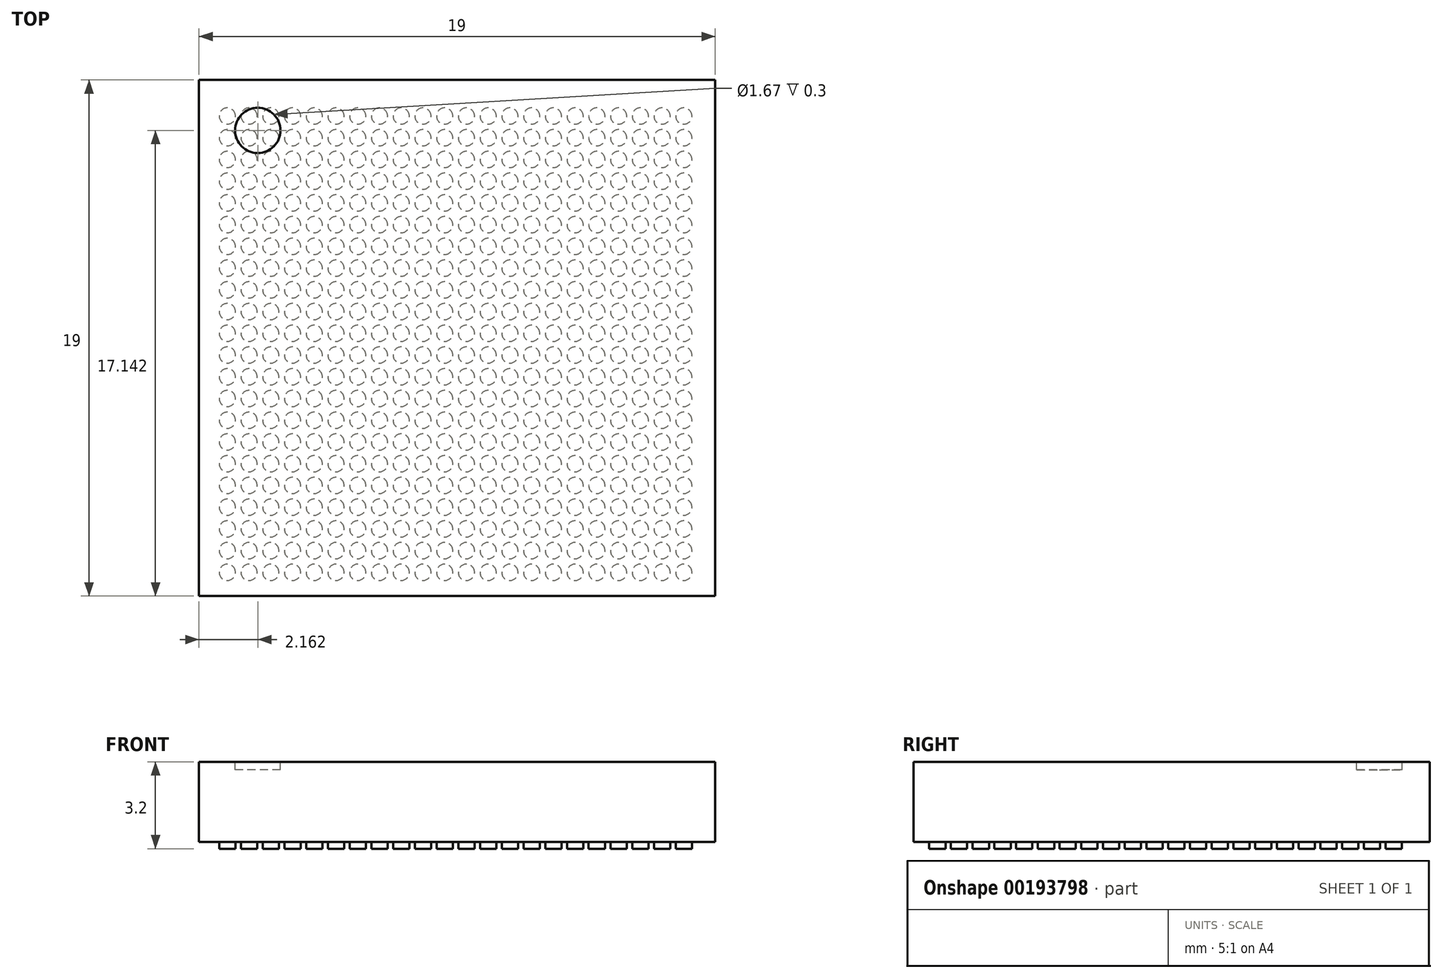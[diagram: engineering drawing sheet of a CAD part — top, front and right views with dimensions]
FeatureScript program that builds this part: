
annotation { "Feature Type Name" : "Feature", "Feature Type Description" : "" }
export const myFeature = defineFeature(function(context is Context, id is Id, definition is map)
    precondition{}
    {
        {
            var Q0;
            Q0=qCreatedBy(makeId("Top.planeOp"),FACE);
            var sketch = newSketch(context, id + "F0", { "sketchPlane" : qUnion([Q0])});
            skLineSegment(sketch, "E0.bottom", {"start": v(9.5, -9.5) * mm, "end": v(-9.5, -9.5) * mm});
            skLineSegment(sketch, "E0.top", {"start": v(9.5, 9.5) * mm, "end": v(-9.5, 9.5) * mm});
            skLineSegment(sketch, "E0.left", {"start": v(9.5, -9.5) * mm, "end": v(9.5, 9.5) * mm});
            skLineSegment(sketch, "E0.right", {"start": v(-9.5, -9.5) * mm, "end": v(-9.5, 9.5) * mm});
            skPoint(sketch, "E0.middle", {"position": v(0, 0) * mm});
            skSolve(sketch);
        }
        {
            var Q0;
            Q0 = qSketchRegion(id + "F0", true);
            extrude(context, id + "F1", {"entities" : qUnion([Q0]), "depth" : 2.95 * mm});
        }
        {
            var Q0;
            Q0=makeQuery(id+"F1.opExtrude","CAP_FACE",FACE,{"disambiguationData":[OSD([sQuery(id+"F0.wireOp",EDGE,"E0.bottom"),sQuery(id+"F0.wireOp",EDGE,"E0.top"),sQuery(id+"F0.wireOp",EDGE,"E0.left"),sQuery(id+"F0.wireOp",EDGE,"E0.right")])],"isStart":false});
            var sketch = newSketch(context, id + "F2", { "sketchPlane" : qUnion([Q0])});
            skCircle(sketch, "E1", {"center": v(-7.34, 7.64) * mm, "radius": 0.84 * mm});
            skSolve(sketch);
        }
        {
            var Q0;
            Q0 = qSketchRegion(id + "F2", true);
            extrude(context, id + "F3", {"entities" : qUnion([Q0]), "operationType" : NewBodyOperationType.REMOVE, "oppositeDirection" : true, "depth" : 0.3 * mm});
        }
        {
            var Q0;
            Q0=makeQuery(id+"F1.opExtrude","CAP_FACE",FACE,{"disambiguationData":[OSD([sQuery(id+"F0.wireOp",EDGE,"E0.bottom"),sQuery(id+"F0.wireOp",EDGE,"E0.top"),sQuery(id+"F0.wireOp",EDGE,"E0.left"),sQuery(id+"F0.wireOp",EDGE,"E0.right")])],"isStart":true});
            var sketch = newSketch(context, id + "F4", { "sketchPlane" : qUnion([Q0])});
            skCircle(sketch, "E2", {"center": v(-8.46, 8.63) * mm, "radius": 0.3 * mm});
            skCircle(sketch, "E3.1.0.0", {"center": v(-7.66, 8.63) * mm, "radius": 0.3 * mm});
            skCircle(sketch, "E3.2.0.0", {"center": v(-6.86, 8.63) * mm, "radius": 0.3 * mm});
            skCircle(sketch, "E3.3.0.0", {"center": v(-6.06, 8.63) * mm, "radius": 0.3 * mm});
            skCircle(sketch, "E3.4.0.0", {"center": v(-5.26, 8.63) * mm, "radius": 0.3 * mm});
            skCircle(sketch, "E3.5.0.0", {"center": v(-4.46, 8.63) * mm, "radius": 0.3 * mm});
            skCircle(sketch, "E3.6.0.0", {"center": v(-3.66, 8.63) * mm, "radius": 0.3 * mm});
            skCircle(sketch, "E3.7.0.0", {"center": v(-2.86, 8.63) * mm, "radius": 0.3 * mm});
            skCircle(sketch, "E3.8.0.0", {"center": v(-2.06, 8.63) * mm, "radius": 0.3 * mm});
            skCircle(sketch, "E3.9.0.0", {"center": v(-1.26, 8.63) * mm, "radius": 0.3 * mm});
            skCircle(sketch, "E3.10.0.0", {"center": v(-0.46, 8.63) * mm, "radius": 0.3 * mm});
            skCircle(sketch, "E3.11.0.0", {"center": v(0.34, 8.63) * mm, "radius": 0.3 * mm});
            skCircle(sketch, "E3.12.0.0", {"center": v(1.14, 8.63) * mm, "radius": 0.3 * mm});
            skCircle(sketch, "E3.13.0.0", {"center": v(1.94, 8.63) * mm, "radius": 0.3 * mm});
            skCircle(sketch, "E3.14.0.0", {"center": v(2.74, 8.63) * mm, "radius": 0.3 * mm});
            skCircle(sketch, "E3.15.0.0", {"center": v(3.54, 8.63) * mm, "radius": 0.3 * mm});
            skCircle(sketch, "E3.16.0.0", {"center": v(4.34, 8.63) * mm, "radius": 0.3 * mm});
            skCircle(sketch, "E3.17.0.0", {"center": v(5.14, 8.63) * mm, "radius": 0.3 * mm});
            skCircle(sketch, "E3.18.0.0", {"center": v(5.94, 8.63) * mm, "radius": 0.3 * mm});
            skCircle(sketch, "E3.19.0.0", {"center": v(6.74, 8.63) * mm, "radius": 0.3 * mm});
            skCircle(sketch, "E3.20.0.0", {"center": v(7.54, 8.63) * mm, "radius": 0.3 * mm});
            skCircle(sketch, "E3.21.0.0", {"center": v(8.34, 8.63) * mm, "radius": 0.3 * mm});
            skLineSegment(sketch, "E3.direction1", {"start": v(-8.46, 8.63) * mm, "end": v(-7.66, 8.63) * mm, "construction": true});
            skCircle(sketch, "E4.1.0.0", {"center": v(-8.46, 7.83) * mm, "radius": 0.3 * mm});
            skCircle(sketch, "E4.1.0.1", {"center": v(-7.66, 7.83) * mm, "radius": 0.3 * mm});
            skCircle(sketch, "E4.1.0.2", {"center": v(-6.86, 7.83) * mm, "radius": 0.3 * mm});
            skCircle(sketch, "E4.1.0.3", {"center": v(-6.06, 7.83) * mm, "radius": 0.3 * mm});
            skCircle(sketch, "E4.1.0.4", {"center": v(-5.26, 7.83) * mm, "radius": 0.3 * mm});
            skCircle(sketch, "E4.1.0.5", {"center": v(-4.46, 7.83) * mm, "radius": 0.3 * mm});
            skCircle(sketch, "E4.1.0.6", {"center": v(-3.66, 7.83) * mm, "radius": 0.3 * mm});
            skCircle(sketch, "E4.1.0.7", {"center": v(-2.86, 7.83) * mm, "radius": 0.3 * mm});
            skCircle(sketch, "E4.1.0.8", {"center": v(-2.06, 7.83) * mm, "radius": 0.3 * mm});
            skCircle(sketch, "E4.1.0.9", {"center": v(-1.26, 7.83) * mm, "radius": 0.3 * mm});
            skCircle(sketch, "E4.1.0.10", {"center": v(-0.46, 7.83) * mm, "radius": 0.3 * mm});
            skCircle(sketch, "E4.1.0.11", {"center": v(0.34, 7.83) * mm, "radius": 0.3 * mm});
            skCircle(sketch, "E4.1.0.12", {"center": v(1.94, 7.83) * mm, "radius": 0.3 * mm});
            skCircle(sketch, "E4.1.0.13", {"center": v(2.74, 7.83) * mm, "radius": 0.3 * mm});
            skCircle(sketch, "E4.1.0.14", {"center": v(1.14, 7.83) * mm, "radius": 0.3 * mm});
            skCircle(sketch, "E4.1.0.15", {"center": v(3.54, 7.83) * mm, "radius": 0.3 * mm});
            skCircle(sketch, "E4.1.0.16", {"center": v(4.34, 7.83) * mm, "radius": 0.3 * mm});
            skCircle(sketch, "E4.1.0.17", {"center": v(5.14, 7.83) * mm, "radius": 0.3 * mm});
            skCircle(sketch, "E4.1.0.18", {"center": v(5.94, 7.83) * mm, "radius": 0.3 * mm});
            skCircle(sketch, "E4.1.0.19", {"center": v(6.74, 7.83) * mm, "radius": 0.3 * mm});
            skCircle(sketch, "E4.1.0.20", {"center": v(7.54, 7.83) * mm, "radius": 0.3 * mm});
            skCircle(sketch, "E4.1.0.21", {"center": v(8.34, 7.83) * mm, "radius": 0.3 * mm});
            skCircle(sketch, "E4.2.0.0", {"center": v(-8.46, 7.03) * mm, "radius": 0.3 * mm});
            skCircle(sketch, "E4.2.0.1", {"center": v(-7.66, 7.03) * mm, "radius": 0.3 * mm});
            skCircle(sketch, "E4.2.0.2", {"center": v(-6.86, 7.03) * mm, "radius": 0.3 * mm});
            skCircle(sketch, "E4.2.0.3", {"center": v(-6.06, 7.03) * mm, "radius": 0.3 * mm});
            skCircle(sketch, "E4.2.0.4", {"center": v(-5.26, 7.03) * mm, "radius": 0.3 * mm});
            skCircle(sketch, "E4.2.0.5", {"center": v(-4.46, 7.03) * mm, "radius": 0.3 * mm});
            skCircle(sketch, "E4.2.0.6", {"center": v(-3.66, 7.03) * mm, "radius": 0.3 * mm});
            skCircle(sketch, "E4.2.0.7", {"center": v(-2.86, 7.03) * mm, "radius": 0.3 * mm});
            skCircle(sketch, "E4.2.0.8", {"center": v(-2.06, 7.03) * mm, "radius": 0.3 * mm});
            skCircle(sketch, "E4.2.0.9", {"center": v(-1.26, 7.03) * mm, "radius": 0.3 * mm});
            skCircle(sketch, "E4.2.0.10", {"center": v(-0.46, 7.03) * mm, "radius": 0.3 * mm});
            skCircle(sketch, "E4.2.0.11", {"center": v(0.34, 7.03) * mm, "radius": 0.3 * mm});
            skCircle(sketch, "E4.2.0.12", {"center": v(1.94, 7.03) * mm, "radius": 0.3 * mm});
            skCircle(sketch, "E4.2.0.13", {"center": v(2.74, 7.03) * mm, "radius": 0.3 * mm});
            skCircle(sketch, "E4.2.0.14", {"center": v(1.14, 7.03) * mm, "radius": 0.3 * mm});
            skCircle(sketch, "E4.2.0.15", {"center": v(3.54, 7.03) * mm, "radius": 0.3 * mm});
            skCircle(sketch, "E4.2.0.16", {"center": v(4.34, 7.03) * mm, "radius": 0.3 * mm});
            skCircle(sketch, "E4.2.0.17", {"center": v(5.14, 7.03) * mm, "radius": 0.3 * mm});
            skCircle(sketch, "E4.2.0.18", {"center": v(5.94, 7.03) * mm, "radius": 0.3 * mm});
            skCircle(sketch, "E4.2.0.19", {"center": v(6.74, 7.03) * mm, "radius": 0.3 * mm});
            skCircle(sketch, "E4.2.0.20", {"center": v(7.54, 7.03) * mm, "radius": 0.3 * mm});
            skCircle(sketch, "E4.2.0.21", {"center": v(8.34, 7.03) * mm, "radius": 0.3 * mm});
            skCircle(sketch, "E4.3.0.0", {"center": v(-8.46, 6.23) * mm, "radius": 0.3 * mm});
            skCircle(sketch, "E4.3.0.1", {"center": v(-7.66, 6.23) * mm, "radius": 0.3 * mm});
            skCircle(sketch, "E4.3.0.2", {"center": v(-6.86, 6.23) * mm, "radius": 0.3 * mm});
            skCircle(sketch, "E4.3.0.3", {"center": v(-6.06, 6.23) * mm, "radius": 0.3 * mm});
            skCircle(sketch, "E4.3.0.4", {"center": v(-5.26, 6.23) * mm, "radius": 0.3 * mm});
            skCircle(sketch, "E4.3.0.5", {"center": v(-4.46, 6.23) * mm, "radius": 0.3 * mm});
            skCircle(sketch, "E4.3.0.6", {"center": v(-3.66, 6.23) * mm, "radius": 0.3 * mm});
            skCircle(sketch, "E4.3.0.7", {"center": v(-2.86, 6.23) * mm, "radius": 0.3 * mm});
            skCircle(sketch, "E4.3.0.8", {"center": v(-2.06, 6.23) * mm, "radius": 0.3 * mm});
            skCircle(sketch, "E4.3.0.9", {"center": v(-1.26, 6.23) * mm, "radius": 0.3 * mm});
            skCircle(sketch, "E4.3.0.10", {"center": v(-0.46, 6.23) * mm, "radius": 0.3 * mm});
            skCircle(sketch, "E4.3.0.11", {"center": v(0.34, 6.23) * mm, "radius": 0.3 * mm});
            skCircle(sketch, "E4.3.0.12", {"center": v(1.94, 6.23) * mm, "radius": 0.3 * mm});
            skCircle(sketch, "E4.3.0.13", {"center": v(2.74, 6.23) * mm, "radius": 0.3 * mm});
            skCircle(sketch, "E4.3.0.14", {"center": v(1.14, 6.23) * mm, "radius": 0.3 * mm});
            skCircle(sketch, "E4.3.0.15", {"center": v(3.54, 6.23) * mm, "radius": 0.3 * mm});
            skCircle(sketch, "E4.3.0.16", {"center": v(4.34, 6.23) * mm, "radius": 0.3 * mm});
            skCircle(sketch, "E4.3.0.17", {"center": v(5.14, 6.23) * mm, "radius": 0.3 * mm});
            skCircle(sketch, "E4.3.0.18", {"center": v(5.94, 6.23) * mm, "radius": 0.3 * mm});
            skCircle(sketch, "E4.3.0.19", {"center": v(6.74, 6.23) * mm, "radius": 0.3 * mm});
            skCircle(sketch, "E4.3.0.20", {"center": v(7.54, 6.23) * mm, "radius": 0.3 * mm});
            skCircle(sketch, "E4.3.0.21", {"center": v(8.34, 6.23) * mm, "radius": 0.3 * mm});
            skCircle(sketch, "E4.4.0.0", {"center": v(-8.46, 5.43) * mm, "radius": 0.3 * mm});
            skCircle(sketch, "E4.4.0.1", {"center": v(-7.66, 5.43) * mm, "radius": 0.3 * mm});
            skCircle(sketch, "E4.4.0.2", {"center": v(-6.86, 5.43) * mm, "radius": 0.3 * mm});
            skCircle(sketch, "E4.4.0.3", {"center": v(-6.06, 5.43) * mm, "radius": 0.3 * mm});
            skCircle(sketch, "E4.4.0.4", {"center": v(-5.26, 5.43) * mm, "radius": 0.3 * mm});
            skCircle(sketch, "E4.4.0.5", {"center": v(-4.46, 5.43) * mm, "radius": 0.3 * mm});
            skCircle(sketch, "E4.4.0.6", {"center": v(-3.66, 5.43) * mm, "radius": 0.3 * mm});
            skCircle(sketch, "E4.4.0.7", {"center": v(-2.86, 5.43) * mm, "radius": 0.3 * mm});
            skCircle(sketch, "E4.4.0.8", {"center": v(-2.06, 5.43) * mm, "radius": 0.3 * mm});
            skCircle(sketch, "E4.4.0.9", {"center": v(-1.26, 5.43) * mm, "radius": 0.3 * mm});
            skCircle(sketch, "E4.4.0.10", {"center": v(-0.46, 5.43) * mm, "radius": 0.3 * mm});
            skCircle(sketch, "E4.4.0.11", {"center": v(0.34, 5.43) * mm, "radius": 0.3 * mm});
            skCircle(sketch, "E4.4.0.12", {"center": v(1.94, 5.43) * mm, "radius": 0.3 * mm});
            skCircle(sketch, "E4.4.0.13", {"center": v(2.74, 5.43) * mm, "radius": 0.3 * mm});
            skCircle(sketch, "E4.4.0.14", {"center": v(1.14, 5.43) * mm, "radius": 0.3 * mm});
            skCircle(sketch, "E4.4.0.15", {"center": v(3.54, 5.43) * mm, "radius": 0.3 * mm});
            skCircle(sketch, "E4.4.0.16", {"center": v(4.34, 5.43) * mm, "radius": 0.3 * mm});
            skCircle(sketch, "E4.4.0.17", {"center": v(5.14, 5.43) * mm, "radius": 0.3 * mm});
            skCircle(sketch, "E4.4.0.18", {"center": v(5.94, 5.43) * mm, "radius": 0.3 * mm});
            skCircle(sketch, "E4.4.0.19", {"center": v(6.74, 5.43) * mm, "radius": 0.3 * mm});
            skCircle(sketch, "E4.4.0.20", {"center": v(7.54, 5.43) * mm, "radius": 0.3 * mm});
            skCircle(sketch, "E4.4.0.21", {"center": v(8.34, 5.43) * mm, "radius": 0.3 * mm});
            skCircle(sketch, "E4.5.0.0", {"center": v(-8.46, 4.63) * mm, "radius": 0.3 * mm});
            skCircle(sketch, "E4.5.0.1", {"center": v(-7.66, 4.63) * mm, "radius": 0.3 * mm});
            skCircle(sketch, "E4.5.0.2", {"center": v(-6.86, 4.63) * mm, "radius": 0.3 * mm});
            skCircle(sketch, "E4.5.0.3", {"center": v(-6.06, 4.63) * mm, "radius": 0.3 * mm});
            skCircle(sketch, "E4.5.0.4", {"center": v(-5.26, 4.63) * mm, "radius": 0.3 * mm});
            skCircle(sketch, "E4.5.0.5", {"center": v(-4.46, 4.63) * mm, "radius": 0.3 * mm});
            skCircle(sketch, "E4.5.0.6", {"center": v(-3.66, 4.63) * mm, "radius": 0.3 * mm});
            skCircle(sketch, "E4.5.0.7", {"center": v(-2.86, 4.63) * mm, "radius": 0.3 * mm});
            skCircle(sketch, "E4.5.0.8", {"center": v(-2.06, 4.63) * mm, "radius": 0.3 * mm});
            skCircle(sketch, "E4.5.0.9", {"center": v(-1.26, 4.63) * mm, "radius": 0.3 * mm});
            skCircle(sketch, "E4.5.0.10", {"center": v(-0.46, 4.63) * mm, "radius": 0.3 * mm});
            skCircle(sketch, "E4.5.0.11", {"center": v(0.34, 4.63) * mm, "radius": 0.3 * mm});
            skCircle(sketch, "E4.5.0.12", {"center": v(1.94, 4.63) * mm, "radius": 0.3 * mm});
            skCircle(sketch, "E4.5.0.13", {"center": v(2.74, 4.63) * mm, "radius": 0.3 * mm});
            skCircle(sketch, "E4.5.0.14", {"center": v(1.14, 4.63) * mm, "radius": 0.3 * mm});
            skCircle(sketch, "E4.5.0.15", {"center": v(3.54, 4.63) * mm, "radius": 0.3 * mm});
            skCircle(sketch, "E4.5.0.16", {"center": v(4.34, 4.63) * mm, "radius": 0.3 * mm});
            skCircle(sketch, "E4.5.0.17", {"center": v(5.14, 4.63) * mm, "radius": 0.3 * mm});
            skCircle(sketch, "E4.5.0.18", {"center": v(5.94, 4.63) * mm, "radius": 0.3 * mm});
            skCircle(sketch, "E4.5.0.19", {"center": v(6.74, 4.63) * mm, "radius": 0.3 * mm});
            skCircle(sketch, "E4.5.0.20", {"center": v(7.54, 4.63) * mm, "radius": 0.3 * mm});
            skCircle(sketch, "E4.5.0.21", {"center": v(8.34, 4.63) * mm, "radius": 0.3 * mm});
            skCircle(sketch, "E4.6.0.0", {"center": v(-8.46, 3.83) * mm, "radius": 0.3 * mm});
            skCircle(sketch, "E4.6.0.1", {"center": v(-7.66, 3.83) * mm, "radius": 0.3 * mm});
            skCircle(sketch, "E4.6.0.2", {"center": v(-6.86, 3.83) * mm, "radius": 0.3 * mm});
            skCircle(sketch, "E4.6.0.3", {"center": v(-6.06, 3.83) * mm, "radius": 0.3 * mm});
            skCircle(sketch, "E4.6.0.4", {"center": v(-5.26, 3.83) * mm, "radius": 0.3 * mm});
            skCircle(sketch, "E4.6.0.5", {"center": v(-4.46, 3.83) * mm, "radius": 0.3 * mm});
            skCircle(sketch, "E4.6.0.6", {"center": v(-3.66, 3.83) * mm, "radius": 0.3 * mm});
            skCircle(sketch, "E4.6.0.7", {"center": v(-2.86, 3.83) * mm, "radius": 0.3 * mm});
            skCircle(sketch, "E4.6.0.8", {"center": v(-2.06, 3.83) * mm, "radius": 0.3 * mm});
            skCircle(sketch, "E4.6.0.9", {"center": v(-1.26, 3.83) * mm, "radius": 0.3 * mm});
            skCircle(sketch, "E4.6.0.10", {"center": v(-0.46, 3.83) * mm, "radius": 0.3 * mm});
            skCircle(sketch, "E4.6.0.11", {"center": v(0.34, 3.83) * mm, "radius": 0.3 * mm});
            skCircle(sketch, "E4.6.0.12", {"center": v(1.94, 3.83) * mm, "radius": 0.3 * mm});
            skCircle(sketch, "E4.6.0.13", {"center": v(2.74, 3.83) * mm, "radius": 0.3 * mm});
            skCircle(sketch, "E4.6.0.14", {"center": v(1.14, 3.83) * mm, "radius": 0.3 * mm});
            skCircle(sketch, "E4.6.0.15", {"center": v(3.54, 3.83) * mm, "radius": 0.3 * mm});
            skCircle(sketch, "E4.6.0.16", {"center": v(4.34, 3.83) * mm, "radius": 0.3 * mm});
            skCircle(sketch, "E4.6.0.17", {"center": v(5.14, 3.83) * mm, "radius": 0.3 * mm});
            skCircle(sketch, "E4.6.0.18", {"center": v(5.94, 3.83) * mm, "radius": 0.3 * mm});
            skCircle(sketch, "E4.6.0.19", {"center": v(6.74, 3.83) * mm, "radius": 0.3 * mm});
            skCircle(sketch, "E4.6.0.20", {"center": v(7.54, 3.83) * mm, "radius": 0.3 * mm});
            skCircle(sketch, "E4.6.0.21", {"center": v(8.34, 3.83) * mm, "radius": 0.3 * mm});
            skCircle(sketch, "E4.7.0.0", {"center": v(-8.46, 3.03) * mm, "radius": 0.3 * mm});
            skCircle(sketch, "E4.7.0.1", {"center": v(-7.66, 3.03) * mm, "radius": 0.3 * mm});
            skCircle(sketch, "E4.7.0.2", {"center": v(-6.86, 3.03) * mm, "radius": 0.3 * mm});
            skCircle(sketch, "E4.7.0.3", {"center": v(-6.06, 3.03) * mm, "radius": 0.3 * mm});
            skCircle(sketch, "E4.7.0.4", {"center": v(-5.26, 3.03) * mm, "radius": 0.3 * mm});
            skCircle(sketch, "E4.7.0.5", {"center": v(-4.46, 3.03) * mm, "radius": 0.3 * mm});
            skCircle(sketch, "E4.7.0.6", {"center": v(-3.66, 3.03) * mm, "radius": 0.3 * mm});
            skCircle(sketch, "E4.7.0.7", {"center": v(-2.86, 3.03) * mm, "radius": 0.3 * mm});
            skCircle(sketch, "E4.7.0.8", {"center": v(-2.06, 3.03) * mm, "radius": 0.3 * mm});
            skCircle(sketch, "E4.7.0.9", {"center": v(-1.26, 3.03) * mm, "radius": 0.3 * mm});
            skCircle(sketch, "E4.7.0.10", {"center": v(-0.46, 3.03) * mm, "radius": 0.3 * mm});
            skCircle(sketch, "E4.7.0.11", {"center": v(0.34, 3.03) * mm, "radius": 0.3 * mm});
            skCircle(sketch, "E4.7.0.12", {"center": v(1.94, 3.03) * mm, "radius": 0.3 * mm});
            skCircle(sketch, "E4.7.0.13", {"center": v(2.74, 3.03) * mm, "radius": 0.3 * mm});
            skCircle(sketch, "E4.7.0.14", {"center": v(1.14, 3.03) * mm, "radius": 0.3 * mm});
            skCircle(sketch, "E4.7.0.15", {"center": v(3.54, 3.03) * mm, "radius": 0.3 * mm});
            skCircle(sketch, "E4.7.0.16", {"center": v(4.34, 3.03) * mm, "radius": 0.3 * mm});
            skCircle(sketch, "E4.7.0.17", {"center": v(5.14, 3.03) * mm, "radius": 0.3 * mm});
            skCircle(sketch, "E4.7.0.18", {"center": v(5.94, 3.03) * mm, "radius": 0.3 * mm});
            skCircle(sketch, "E4.7.0.19", {"center": v(6.74, 3.03) * mm, "radius": 0.3 * mm});
            skCircle(sketch, "E4.7.0.20", {"center": v(7.54, 3.03) * mm, "radius": 0.3 * mm});
            skCircle(sketch, "E4.7.0.21", {"center": v(8.34, 3.03) * mm, "radius": 0.3 * mm});
            skCircle(sketch, "E4.8.0.0", {"center": v(-8.46, 2.23) * mm, "radius": 0.3 * mm});
            skCircle(sketch, "E4.8.0.1", {"center": v(-7.66, 2.23) * mm, "radius": 0.3 * mm});
            skCircle(sketch, "E4.8.0.2", {"center": v(-6.86, 2.23) * mm, "radius": 0.3 * mm});
            skCircle(sketch, "E4.8.0.3", {"center": v(-6.06, 2.23) * mm, "radius": 0.3 * mm});
            skCircle(sketch, "E4.8.0.4", {"center": v(-5.26, 2.23) * mm, "radius": 0.3 * mm});
            skCircle(sketch, "E4.8.0.5", {"center": v(-4.46, 2.23) * mm, "radius": 0.3 * mm});
            skCircle(sketch, "E4.8.0.6", {"center": v(-3.66, 2.23) * mm, "radius": 0.3 * mm});
            skCircle(sketch, "E4.8.0.7", {"center": v(-2.86, 2.23) * mm, "radius": 0.3 * mm});
            skCircle(sketch, "E4.8.0.8", {"center": v(-2.06, 2.23) * mm, "radius": 0.3 * mm});
            skCircle(sketch, "E4.8.0.9", {"center": v(-1.26, 2.23) * mm, "radius": 0.3 * mm});
            skCircle(sketch, "E4.8.0.10", {"center": v(-0.46, 2.23) * mm, "radius": 0.3 * mm});
            skCircle(sketch, "E4.8.0.11", {"center": v(0.34, 2.23) * mm, "radius": 0.3 * mm});
            skCircle(sketch, "E4.8.0.12", {"center": v(1.94, 2.23) * mm, "radius": 0.3 * mm});
            skCircle(sketch, "E4.8.0.13", {"center": v(2.74, 2.23) * mm, "radius": 0.3 * mm});
            skCircle(sketch, "E4.8.0.14", {"center": v(1.14, 2.23) * mm, "radius": 0.3 * mm});
            skCircle(sketch, "E4.8.0.15", {"center": v(3.54, 2.23) * mm, "radius": 0.3 * mm});
            skCircle(sketch, "E4.8.0.16", {"center": v(4.34, 2.23) * mm, "radius": 0.3 * mm});
            skCircle(sketch, "E4.8.0.17", {"center": v(5.14, 2.23) * mm, "radius": 0.3 * mm});
            skCircle(sketch, "E4.8.0.18", {"center": v(5.94, 2.23) * mm, "radius": 0.3 * mm});
            skCircle(sketch, "E4.8.0.19", {"center": v(6.74, 2.23) * mm, "radius": 0.3 * mm});
            skCircle(sketch, "E4.8.0.20", {"center": v(7.54, 2.23) * mm, "radius": 0.3 * mm});
            skCircle(sketch, "E4.8.0.21", {"center": v(8.34, 2.23) * mm, "radius": 0.3 * mm});
            skCircle(sketch, "E4.9.0.0", {"center": v(-8.46, 1.43) * mm, "radius": 0.3 * mm});
            skCircle(sketch, "E4.9.0.1", {"center": v(-7.66, 1.43) * mm, "radius": 0.3 * mm});
            skCircle(sketch, "E4.9.0.2", {"center": v(-6.86, 1.43) * mm, "radius": 0.3 * mm});
            skCircle(sketch, "E4.9.0.3", {"center": v(-6.06, 1.43) * mm, "radius": 0.3 * mm});
            skCircle(sketch, "E4.9.0.4", {"center": v(-5.26, 1.43) * mm, "radius": 0.3 * mm});
            skCircle(sketch, "E4.9.0.5", {"center": v(-4.46, 1.43) * mm, "radius": 0.3 * mm});
            skCircle(sketch, "E4.9.0.6", {"center": v(-3.66, 1.43) * mm, "radius": 0.3 * mm});
            skCircle(sketch, "E4.9.0.7", {"center": v(-2.86, 1.43) * mm, "radius": 0.3 * mm});
            skCircle(sketch, "E4.9.0.8", {"center": v(-2.06, 1.43) * mm, "radius": 0.3 * mm});
            skCircle(sketch, "E4.9.0.9", {"center": v(-1.26, 1.43) * mm, "radius": 0.3 * mm});
            skCircle(sketch, "E4.9.0.10", {"center": v(-0.46, 1.43) * mm, "radius": 0.3 * mm});
            skCircle(sketch, "E4.9.0.11", {"center": v(0.34, 1.43) * mm, "radius": 0.3 * mm});
            skCircle(sketch, "E4.9.0.12", {"center": v(1.94, 1.43) * mm, "radius": 0.3 * mm});
            skCircle(sketch, "E4.9.0.13", {"center": v(2.74, 1.43) * mm, "radius": 0.3 * mm});
            skCircle(sketch, "E4.9.0.14", {"center": v(1.14, 1.43) * mm, "radius": 0.3 * mm});
            skCircle(sketch, "E4.9.0.15", {"center": v(3.54, 1.43) * mm, "radius": 0.3 * mm});
            skCircle(sketch, "E4.9.0.16", {"center": v(4.34, 1.43) * mm, "radius": 0.3 * mm});
            skCircle(sketch, "E4.9.0.17", {"center": v(5.14, 1.43) * mm, "radius": 0.3 * mm});
            skCircle(sketch, "E4.9.0.18", {"center": v(5.94, 1.43) * mm, "radius": 0.3 * mm});
            skCircle(sketch, "E4.9.0.19", {"center": v(6.74, 1.43) * mm, "radius": 0.3 * mm});
            skCircle(sketch, "E4.9.0.20", {"center": v(7.54, 1.43) * mm, "radius": 0.3 * mm});
            skCircle(sketch, "E4.9.0.21", {"center": v(8.34, 1.43) * mm, "radius": 0.3 * mm});
            skCircle(sketch, "E4.10.0.0", {"center": v(-8.46, 0.63) * mm, "radius": 0.3 * mm});
            skCircle(sketch, "E4.10.0.1", {"center": v(-7.66, 0.63) * mm, "radius": 0.3 * mm});
            skCircle(sketch, "E4.10.0.2", {"center": v(-6.86, 0.63) * mm, "radius": 0.3 * mm});
            skCircle(sketch, "E4.10.0.3", {"center": v(-6.06, 0.63) * mm, "radius": 0.3 * mm});
            skCircle(sketch, "E4.10.0.4", {"center": v(-5.26, 0.63) * mm, "radius": 0.3 * mm});
            skCircle(sketch, "E4.10.0.5", {"center": v(-4.46, 0.63) * mm, "radius": 0.3 * mm});
            skCircle(sketch, "E4.10.0.6", {"center": v(-3.66, 0.63) * mm, "radius": 0.3 * mm});
            skCircle(sketch, "E4.10.0.7", {"center": v(-2.86, 0.63) * mm, "radius": 0.3 * mm});
            skCircle(sketch, "E4.10.0.8", {"center": v(-2.06, 0.63) * mm, "radius": 0.3 * mm});
            skCircle(sketch, "E4.10.0.9", {"center": v(-1.26, 0.63) * mm, "radius": 0.3 * mm});
            skCircle(sketch, "E4.10.0.10", {"center": v(-0.46, 0.63) * mm, "radius": 0.3 * mm});
            skCircle(sketch, "E4.10.0.11", {"center": v(0.34, 0.63) * mm, "radius": 0.3 * mm});
            skCircle(sketch, "E4.10.0.12", {"center": v(1.94, 0.63) * mm, "radius": 0.3 * mm});
            skCircle(sketch, "E4.10.0.13", {"center": v(2.74, 0.63) * mm, "radius": 0.3 * mm});
            skCircle(sketch, "E4.10.0.14", {"center": v(1.14, 0.63) * mm, "radius": 0.3 * mm});
            skCircle(sketch, "E4.10.0.15", {"center": v(3.54, 0.63) * mm, "radius": 0.3 * mm});
            skCircle(sketch, "E4.10.0.16", {"center": v(4.34, 0.63) * mm, "radius": 0.3 * mm});
            skCircle(sketch, "E4.10.0.17", {"center": v(5.14, 0.63) * mm, "radius": 0.3 * mm});
            skCircle(sketch, "E4.10.0.18", {"center": v(5.94, 0.63) * mm, "radius": 0.3 * mm});
            skCircle(sketch, "E4.10.0.19", {"center": v(6.74, 0.63) * mm, "radius": 0.3 * mm});
            skCircle(sketch, "E4.10.0.20", {"center": v(7.54, 0.63) * mm, "radius": 0.3 * mm});
            skCircle(sketch, "E4.10.0.21", {"center": v(8.34, 0.63) * mm, "radius": 0.3 * mm});
            skCircle(sketch, "E4.11.0.0", {"center": v(-8.46, -0.17) * mm, "radius": 0.3 * mm});
            skCircle(sketch, "E4.11.0.1", {"center": v(-7.66, -0.17) * mm, "radius": 0.3 * mm});
            skCircle(sketch, "E4.11.0.2", {"center": v(-6.86, -0.17) * mm, "radius": 0.3 * mm});
            skCircle(sketch, "E4.11.0.3", {"center": v(-6.06, -0.17) * mm, "radius": 0.3 * mm});
            skCircle(sketch, "E4.11.0.4", {"center": v(-5.26, -0.17) * mm, "radius": 0.3 * mm});
            skCircle(sketch, "E4.11.0.5", {"center": v(-4.46, -0.17) * mm, "radius": 0.3 * mm});
            skCircle(sketch, "E4.11.0.6", {"center": v(-3.66, -0.17) * mm, "radius": 0.3 * mm});
            skCircle(sketch, "E4.11.0.7", {"center": v(-2.86, -0.17) * mm, "radius": 0.3 * mm});
            skCircle(sketch, "E4.11.0.8", {"center": v(-2.06, -0.17) * mm, "radius": 0.3 * mm});
            skCircle(sketch, "E4.11.0.9", {"center": v(-1.26, -0.17) * mm, "radius": 0.3 * mm});
            skCircle(sketch, "E4.11.0.10", {"center": v(-0.46, -0.17) * mm, "radius": 0.3 * mm});
            skCircle(sketch, "E4.11.0.11", {"center": v(0.34, -0.17) * mm, "radius": 0.3 * mm});
            skCircle(sketch, "E4.11.0.12", {"center": v(1.94, -0.17) * mm, "radius": 0.3 * mm});
            skCircle(sketch, "E4.11.0.13", {"center": v(2.74, -0.17) * mm, "radius": 0.3 * mm});
            skCircle(sketch, "E4.11.0.14", {"center": v(1.14, -0.17) * mm, "radius": 0.3 * mm});
            skCircle(sketch, "E4.11.0.15", {"center": v(3.54, -0.17) * mm, "radius": 0.3 * mm});
            skCircle(sketch, "E4.11.0.16", {"center": v(4.34, -0.17) * mm, "radius": 0.3 * mm});
            skCircle(sketch, "E4.11.0.17", {"center": v(5.14, -0.17) * mm, "radius": 0.3 * mm});
            skCircle(sketch, "E4.11.0.18", {"center": v(5.94, -0.17) * mm, "radius": 0.3 * mm});
            skCircle(sketch, "E4.11.0.19", {"center": v(6.74, -0.17) * mm, "radius": 0.3 * mm});
            skCircle(sketch, "E4.11.0.20", {"center": v(7.54, -0.17) * mm, "radius": 0.3 * mm});
            skCircle(sketch, "E4.11.0.21", {"center": v(8.34, -0.17) * mm, "radius": 0.3 * mm});
            skCircle(sketch, "E4.12.0.0", {"center": v(-8.46, -0.97) * mm, "radius": 0.3 * mm});
            skCircle(sketch, "E4.12.0.1", {"center": v(-7.66, -0.97) * mm, "radius": 0.3 * mm});
            skCircle(sketch, "E4.12.0.2", {"center": v(-6.86, -0.97) * mm, "radius": 0.3 * mm});
            skCircle(sketch, "E4.12.0.3", {"center": v(-6.06, -0.97) * mm, "radius": 0.3 * mm});
            skCircle(sketch, "E4.12.0.4", {"center": v(-5.26, -0.97) * mm, "radius": 0.3 * mm});
            skCircle(sketch, "E4.12.0.5", {"center": v(-4.46, -0.97) * mm, "radius": 0.3 * mm});
            skCircle(sketch, "E4.12.0.6", {"center": v(-3.66, -0.97) * mm, "radius": 0.3 * mm});
            skCircle(sketch, "E4.12.0.7", {"center": v(-2.86, -0.97) * mm, "radius": 0.3 * mm});
            skCircle(sketch, "E4.12.0.8", {"center": v(-2.06, -0.97) * mm, "radius": 0.3 * mm});
            skCircle(sketch, "E4.12.0.9", {"center": v(-1.26, -0.97) * mm, "radius": 0.3 * mm});
            skCircle(sketch, "E4.12.0.10", {"center": v(-0.46, -0.97) * mm, "radius": 0.3 * mm});
            skCircle(sketch, "E4.12.0.11", {"center": v(0.34, -0.97) * mm, "radius": 0.3 * mm});
            skCircle(sketch, "E4.12.0.12", {"center": v(1.94, -0.97) * mm, "radius": 0.3 * mm});
            skCircle(sketch, "E4.12.0.13", {"center": v(2.74, -0.97) * mm, "radius": 0.3 * mm});
            skCircle(sketch, "E4.12.0.14", {"center": v(1.14, -0.97) * mm, "radius": 0.3 * mm});
            skCircle(sketch, "E4.12.0.15", {"center": v(3.54, -0.97) * mm, "radius": 0.3 * mm});
            skCircle(sketch, "E4.12.0.16", {"center": v(4.34, -0.97) * mm, "radius": 0.3 * mm});
            skCircle(sketch, "E4.12.0.17", {"center": v(5.14, -0.97) * mm, "radius": 0.3 * mm});
            skCircle(sketch, "E4.12.0.18", {"center": v(5.94, -0.97) * mm, "radius": 0.3 * mm});
            skCircle(sketch, "E4.12.0.19", {"center": v(6.74, -0.97) * mm, "radius": 0.3 * mm});
            skCircle(sketch, "E4.12.0.20", {"center": v(7.54, -0.97) * mm, "radius": 0.3 * mm});
            skCircle(sketch, "E4.12.0.21", {"center": v(8.34, -0.97) * mm, "radius": 0.3 * mm});
            skCircle(sketch, "E4.13.0.0", {"center": v(-8.46, -1.77) * mm, "radius": 0.3 * mm});
            skCircle(sketch, "E4.13.0.1", {"center": v(-7.66, -1.77) * mm, "radius": 0.3 * mm});
            skCircle(sketch, "E4.13.0.2", {"center": v(-6.86, -1.77) * mm, "radius": 0.3 * mm});
            skCircle(sketch, "E4.13.0.3", {"center": v(-6.06, -1.77) * mm, "radius": 0.3 * mm});
            skCircle(sketch, "E4.13.0.4", {"center": v(-5.26, -1.77) * mm, "radius": 0.3 * mm});
            skCircle(sketch, "E4.13.0.5", {"center": v(-4.46, -1.77) * mm, "radius": 0.3 * mm});
            skCircle(sketch, "E4.13.0.6", {"center": v(-3.66, -1.77) * mm, "radius": 0.3 * mm});
            skCircle(sketch, "E4.13.0.7", {"center": v(-2.86, -1.77) * mm, "radius": 0.3 * mm});
            skCircle(sketch, "E4.13.0.8", {"center": v(-2.06, -1.77) * mm, "radius": 0.3 * mm});
            skCircle(sketch, "E4.13.0.9", {"center": v(-1.26, -1.77) * mm, "radius": 0.3 * mm});
            skCircle(sketch, "E4.13.0.10", {"center": v(-0.46, -1.77) * mm, "radius": 0.3 * mm});
            skCircle(sketch, "E4.13.0.11", {"center": v(0.34, -1.77) * mm, "radius": 0.3 * mm});
            skCircle(sketch, "E4.13.0.12", {"center": v(1.94, -1.77) * mm, "radius": 0.3 * mm});
            skCircle(sketch, "E4.13.0.13", {"center": v(2.74, -1.77) * mm, "radius": 0.3 * mm});
            skCircle(sketch, "E4.13.0.14", {"center": v(1.14, -1.77) * mm, "radius": 0.3 * mm});
            skCircle(sketch, "E4.13.0.15", {"center": v(3.54, -1.77) * mm, "radius": 0.3 * mm});
            skCircle(sketch, "E4.13.0.16", {"center": v(4.34, -1.77) * mm, "radius": 0.3 * mm});
            skCircle(sketch, "E4.13.0.17", {"center": v(5.14, -1.77) * mm, "radius": 0.3 * mm});
            skCircle(sketch, "E4.13.0.18", {"center": v(5.94, -1.77) * mm, "radius": 0.3 * mm});
            skCircle(sketch, "E4.13.0.19", {"center": v(6.74, -1.77) * mm, "radius": 0.3 * mm});
            skCircle(sketch, "E4.13.0.20", {"center": v(7.54, -1.77) * mm, "radius": 0.3 * mm});
            skCircle(sketch, "E4.13.0.21", {"center": v(8.34, -1.77) * mm, "radius": 0.3 * mm});
            skCircle(sketch, "E4.14.0.0", {"center": v(-8.46, -2.57) * mm, "radius": 0.3 * mm});
            skCircle(sketch, "E4.14.0.1", {"center": v(-7.66, -2.57) * mm, "radius": 0.3 * mm});
            skCircle(sketch, "E4.14.0.2", {"center": v(-6.86, -2.57) * mm, "radius": 0.3 * mm});
            skCircle(sketch, "E4.14.0.3", {"center": v(-6.06, -2.57) * mm, "radius": 0.3 * mm});
            skCircle(sketch, "E4.14.0.4", {"center": v(-5.26, -2.57) * mm, "radius": 0.3 * mm});
            skCircle(sketch, "E4.14.0.5", {"center": v(-4.46, -2.57) * mm, "radius": 0.3 * mm});
            skCircle(sketch, "E4.14.0.6", {"center": v(-3.66, -2.57) * mm, "radius": 0.3 * mm});
            skCircle(sketch, "E4.14.0.7", {"center": v(-2.86, -2.57) * mm, "radius": 0.3 * mm});
            skCircle(sketch, "E4.14.0.8", {"center": v(-2.06, -2.57) * mm, "radius": 0.3 * mm});
            skCircle(sketch, "E4.14.0.9", {"center": v(-1.26, -2.57) * mm, "radius": 0.3 * mm});
            skCircle(sketch, "E4.14.0.10", {"center": v(-0.46, -2.57) * mm, "radius": 0.3 * mm});
            skCircle(sketch, "E4.14.0.11", {"center": v(0.34, -2.57) * mm, "radius": 0.3 * mm});
            skCircle(sketch, "E4.14.0.12", {"center": v(1.94, -2.57) * mm, "radius": 0.3 * mm});
            skCircle(sketch, "E4.14.0.13", {"center": v(2.74, -2.57) * mm, "radius": 0.3 * mm});
            skCircle(sketch, "E4.14.0.14", {"center": v(1.14, -2.57) * mm, "radius": 0.3 * mm});
            skCircle(sketch, "E4.14.0.15", {"center": v(3.54, -2.57) * mm, "radius": 0.3 * mm});
            skCircle(sketch, "E4.14.0.16", {"center": v(4.34, -2.57) * mm, "radius": 0.3 * mm});
            skCircle(sketch, "E4.14.0.17", {"center": v(5.14, -2.57) * mm, "radius": 0.3 * mm});
            skCircle(sketch, "E4.14.0.18", {"center": v(5.94, -2.57) * mm, "radius": 0.3 * mm});
            skCircle(sketch, "E4.14.0.19", {"center": v(6.74, -2.57) * mm, "radius": 0.3 * mm});
            skCircle(sketch, "E4.14.0.20", {"center": v(7.54, -2.57) * mm, "radius": 0.3 * mm});
            skCircle(sketch, "E4.14.0.21", {"center": v(8.34, -2.57) * mm, "radius": 0.3 * mm});
            skCircle(sketch, "E4.15.0.0", {"center": v(-8.46, -3.37) * mm, "radius": 0.3 * mm});
            skCircle(sketch, "E4.15.0.1", {"center": v(-7.66, -3.37) * mm, "radius": 0.3 * mm});
            skCircle(sketch, "E4.15.0.2", {"center": v(-6.86, -3.37) * mm, "radius": 0.3 * mm});
            skCircle(sketch, "E4.15.0.3", {"center": v(-6.06, -3.37) * mm, "radius": 0.3 * mm});
            skCircle(sketch, "E4.15.0.4", {"center": v(-5.26, -3.37) * mm, "radius": 0.3 * mm});
            skCircle(sketch, "E4.15.0.5", {"center": v(-4.46, -3.37) * mm, "radius": 0.3 * mm});
            skCircle(sketch, "E4.15.0.6", {"center": v(-3.66, -3.37) * mm, "radius": 0.3 * mm});
            skCircle(sketch, "E4.15.0.7", {"center": v(-2.86, -3.37) * mm, "radius": 0.3 * mm});
            skCircle(sketch, "E4.15.0.8", {"center": v(-2.06, -3.37) * mm, "radius": 0.3 * mm});
            skCircle(sketch, "E4.15.0.9", {"center": v(-1.26, -3.37) * mm, "radius": 0.3 * mm});
            skCircle(sketch, "E4.15.0.10", {"center": v(-0.46, -3.37) * mm, "radius": 0.3 * mm});
            skCircle(sketch, "E4.15.0.11", {"center": v(0.34, -3.37) * mm, "radius": 0.3 * mm});
            skCircle(sketch, "E4.15.0.12", {"center": v(1.94, -3.37) * mm, "radius": 0.3 * mm});
            skCircle(sketch, "E4.15.0.13", {"center": v(2.74, -3.37) * mm, "radius": 0.3 * mm});
            skCircle(sketch, "E4.15.0.14", {"center": v(1.14, -3.37) * mm, "radius": 0.3 * mm});
            skCircle(sketch, "E4.15.0.15", {"center": v(3.54, -3.37) * mm, "radius": 0.3 * mm});
            skCircle(sketch, "E4.15.0.16", {"center": v(4.34, -3.37) * mm, "radius": 0.3 * mm});
            skCircle(sketch, "E4.15.0.17", {"center": v(5.14, -3.37) * mm, "radius": 0.3 * mm});
            skCircle(sketch, "E4.15.0.18", {"center": v(5.94, -3.37) * mm, "radius": 0.3 * mm});
            skCircle(sketch, "E4.15.0.19", {"center": v(6.74, -3.37) * mm, "radius": 0.3 * mm});
            skCircle(sketch, "E4.15.0.20", {"center": v(7.54, -3.37) * mm, "radius": 0.3 * mm});
            skCircle(sketch, "E4.15.0.21", {"center": v(8.34, -3.37) * mm, "radius": 0.3 * mm});
            skCircle(sketch, "E4.16.0.0", {"center": v(-8.46, -4.17) * mm, "radius": 0.3 * mm});
            skCircle(sketch, "E4.16.0.1", {"center": v(-7.66, -4.17) * mm, "radius": 0.3 * mm});
            skCircle(sketch, "E4.16.0.2", {"center": v(-6.86, -4.17) * mm, "radius": 0.3 * mm});
            skCircle(sketch, "E4.16.0.3", {"center": v(-6.06, -4.17) * mm, "radius": 0.3 * mm});
            skCircle(sketch, "E4.16.0.4", {"center": v(-5.26, -4.17) * mm, "radius": 0.3 * mm});
            skCircle(sketch, "E4.16.0.5", {"center": v(-4.46, -4.17) * mm, "radius": 0.3 * mm});
            skCircle(sketch, "E4.16.0.6", {"center": v(-3.66, -4.17) * mm, "radius": 0.3 * mm});
            skCircle(sketch, "E4.16.0.7", {"center": v(-2.86, -4.17) * mm, "radius": 0.3 * mm});
            skCircle(sketch, "E4.16.0.8", {"center": v(-2.06, -4.17) * mm, "radius": 0.3 * mm});
            skCircle(sketch, "E4.16.0.9", {"center": v(-1.26, -4.17) * mm, "radius": 0.3 * mm});
            skCircle(sketch, "E4.16.0.10", {"center": v(-0.46, -4.17) * mm, "radius": 0.3 * mm});
            skCircle(sketch, "E4.16.0.11", {"center": v(0.34, -4.17) * mm, "radius": 0.3 * mm});
            skCircle(sketch, "E4.16.0.12", {"center": v(1.94, -4.17) * mm, "radius": 0.3 * mm});
            skCircle(sketch, "E4.16.0.13", {"center": v(2.74, -4.17) * mm, "radius": 0.3 * mm});
            skCircle(sketch, "E4.16.0.14", {"center": v(1.14, -4.17) * mm, "radius": 0.3 * mm});
            skCircle(sketch, "E4.16.0.15", {"center": v(3.54, -4.17) * mm, "radius": 0.3 * mm});
            skCircle(sketch, "E4.16.0.16", {"center": v(4.34, -4.17) * mm, "radius": 0.3 * mm});
            skCircle(sketch, "E4.16.0.17", {"center": v(5.14, -4.17) * mm, "radius": 0.3 * mm});
            skCircle(sketch, "E4.16.0.18", {"center": v(5.94, -4.17) * mm, "radius": 0.3 * mm});
            skCircle(sketch, "E4.16.0.19", {"center": v(6.74, -4.17) * mm, "radius": 0.3 * mm});
            skCircle(sketch, "E4.16.0.20", {"center": v(7.54, -4.17) * mm, "radius": 0.3 * mm});
            skCircle(sketch, "E4.16.0.21", {"center": v(8.34, -4.17) * mm, "radius": 0.3 * mm});
            skCircle(sketch, "E4.17.0.0", {"center": v(-8.46, -4.97) * mm, "radius": 0.3 * mm});
            skCircle(sketch, "E4.17.0.1", {"center": v(-7.66, -4.97) * mm, "radius": 0.3 * mm});
            skCircle(sketch, "E4.17.0.2", {"center": v(-6.86, -4.97) * mm, "radius": 0.3 * mm});
            skCircle(sketch, "E4.17.0.3", {"center": v(-6.06, -4.97) * mm, "radius": 0.3 * mm});
            skCircle(sketch, "E4.17.0.4", {"center": v(-5.26, -4.97) * mm, "radius": 0.3 * mm});
            skCircle(sketch, "E4.17.0.5", {"center": v(-4.46, -4.97) * mm, "radius": 0.3 * mm});
            skCircle(sketch, "E4.17.0.6", {"center": v(-3.66, -4.97) * mm, "radius": 0.3 * mm});
            skCircle(sketch, "E4.17.0.7", {"center": v(-2.86, -4.97) * mm, "radius": 0.3 * mm});
            skCircle(sketch, "E4.17.0.8", {"center": v(-2.06, -4.97) * mm, "radius": 0.3 * mm});
            skCircle(sketch, "E4.17.0.9", {"center": v(-1.26, -4.97) * mm, "radius": 0.3 * mm});
            skCircle(sketch, "E4.17.0.10", {"center": v(-0.46, -4.97) * mm, "radius": 0.3 * mm});
            skCircle(sketch, "E4.17.0.11", {"center": v(0.34, -4.97) * mm, "radius": 0.3 * mm});
            skCircle(sketch, "E4.17.0.12", {"center": v(1.94, -4.97) * mm, "radius": 0.3 * mm});
            skCircle(sketch, "E4.17.0.13", {"center": v(2.74, -4.97) * mm, "radius": 0.3 * mm});
            skCircle(sketch, "E4.17.0.14", {"center": v(1.14, -4.97) * mm, "radius": 0.3 * mm});
            skCircle(sketch, "E4.17.0.15", {"center": v(3.54, -4.97) * mm, "radius": 0.3 * mm});
            skCircle(sketch, "E4.17.0.16", {"center": v(4.34, -4.97) * mm, "radius": 0.3 * mm});
            skCircle(sketch, "E4.17.0.17", {"center": v(5.14, -4.97) * mm, "radius": 0.3 * mm});
            skCircle(sketch, "E4.17.0.18", {"center": v(5.94, -4.97) * mm, "radius": 0.3 * mm});
            skCircle(sketch, "E4.17.0.19", {"center": v(6.74, -4.97) * mm, "radius": 0.3 * mm});
            skCircle(sketch, "E4.17.0.20", {"center": v(7.54, -4.97) * mm, "radius": 0.3 * mm});
            skCircle(sketch, "E4.17.0.21", {"center": v(8.34, -4.97) * mm, "radius": 0.3 * mm});
            skCircle(sketch, "E4.18.0.0", {"center": v(-8.46, -5.77) * mm, "radius": 0.3 * mm});
            skCircle(sketch, "E4.18.0.1", {"center": v(-7.66, -5.77) * mm, "radius": 0.3 * mm});
            skCircle(sketch, "E4.18.0.2", {"center": v(-6.86, -5.77) * mm, "radius": 0.3 * mm});
            skCircle(sketch, "E4.18.0.3", {"center": v(-6.06, -5.77) * mm, "radius": 0.3 * mm});
            skCircle(sketch, "E4.18.0.4", {"center": v(-5.26, -5.77) * mm, "radius": 0.3 * mm});
            skCircle(sketch, "E4.18.0.5", {"center": v(-4.46, -5.77) * mm, "radius": 0.3 * mm});
            skCircle(sketch, "E4.18.0.6", {"center": v(-3.66, -5.77) * mm, "radius": 0.3 * mm});
            skCircle(sketch, "E4.18.0.7", {"center": v(-2.86, -5.77) * mm, "radius": 0.3 * mm});
            skCircle(sketch, "E4.18.0.8", {"center": v(-2.06, -5.77) * mm, "radius": 0.3 * mm});
            skCircle(sketch, "E4.18.0.9", {"center": v(-1.26, -5.77) * mm, "radius": 0.3 * mm});
            skCircle(sketch, "E4.18.0.10", {"center": v(-0.46, -5.77) * mm, "radius": 0.3 * mm});
            skCircle(sketch, "E4.18.0.11", {"center": v(0.34, -5.77) * mm, "radius": 0.3 * mm});
            skCircle(sketch, "E4.18.0.12", {"center": v(1.94, -5.77) * mm, "radius": 0.3 * mm});
            skCircle(sketch, "E4.18.0.13", {"center": v(2.74, -5.77) * mm, "radius": 0.3 * mm});
            skCircle(sketch, "E4.18.0.14", {"center": v(1.14, -5.77) * mm, "radius": 0.3 * mm});
            skCircle(sketch, "E4.18.0.15", {"center": v(3.54, -5.77) * mm, "radius": 0.3 * mm});
            skCircle(sketch, "E4.18.0.16", {"center": v(4.34, -5.77) * mm, "radius": 0.3 * mm});
            skCircle(sketch, "E4.18.0.17", {"center": v(5.14, -5.77) * mm, "radius": 0.3 * mm});
            skCircle(sketch, "E4.18.0.18", {"center": v(5.94, -5.77) * mm, "radius": 0.3 * mm});
            skCircle(sketch, "E4.18.0.19", {"center": v(6.74, -5.77) * mm, "radius": 0.3 * mm});
            skCircle(sketch, "E4.18.0.20", {"center": v(7.54, -5.77) * mm, "radius": 0.3 * mm});
            skCircle(sketch, "E4.18.0.21", {"center": v(8.34, -5.77) * mm, "radius": 0.3 * mm});
            skCircle(sketch, "E4.19.0.0", {"center": v(-8.46, -6.57) * mm, "radius": 0.3 * mm});
            skCircle(sketch, "E4.19.0.1", {"center": v(-7.66, -6.57) * mm, "radius": 0.3 * mm});
            skCircle(sketch, "E4.19.0.2", {"center": v(-6.86, -6.57) * mm, "radius": 0.3 * mm});
            skCircle(sketch, "E4.19.0.3", {"center": v(-6.06, -6.57) * mm, "radius": 0.3 * mm});
            skCircle(sketch, "E4.19.0.4", {"center": v(-5.26, -6.57) * mm, "radius": 0.3 * mm});
            skCircle(sketch, "E4.19.0.5", {"center": v(-4.46, -6.57) * mm, "radius": 0.3 * mm});
            skCircle(sketch, "E4.19.0.6", {"center": v(-3.66, -6.57) * mm, "radius": 0.3 * mm});
            skCircle(sketch, "E4.19.0.7", {"center": v(-2.86, -6.57) * mm, "radius": 0.3 * mm});
            skCircle(sketch, "E4.19.0.8", {"center": v(-2.06, -6.57) * mm, "radius": 0.3 * mm});
            skCircle(sketch, "E4.19.0.9", {"center": v(-1.26, -6.57) * mm, "radius": 0.3 * mm});
            skCircle(sketch, "E4.19.0.10", {"center": v(-0.46, -6.57) * mm, "radius": 0.3 * mm});
            skCircle(sketch, "E4.19.0.11", {"center": v(0.34, -6.57) * mm, "radius": 0.3 * mm});
            skCircle(sketch, "E4.19.0.12", {"center": v(1.94, -6.57) * mm, "radius": 0.3 * mm});
            skCircle(sketch, "E4.19.0.13", {"center": v(2.74, -6.57) * mm, "radius": 0.3 * mm});
            skCircle(sketch, "E4.19.0.14", {"center": v(1.14, -6.57) * mm, "radius": 0.3 * mm});
            skCircle(sketch, "E4.19.0.15", {"center": v(3.54, -6.57) * mm, "radius": 0.3 * mm});
            skCircle(sketch, "E4.19.0.16", {"center": v(4.34, -6.57) * mm, "radius": 0.3 * mm});
            skCircle(sketch, "E4.19.0.17", {"center": v(5.14, -6.57) * mm, "radius": 0.3 * mm});
            skCircle(sketch, "E4.19.0.18", {"center": v(5.94, -6.57) * mm, "radius": 0.3 * mm});
            skCircle(sketch, "E4.19.0.19", {"center": v(6.74, -6.57) * mm, "radius": 0.3 * mm});
            skCircle(sketch, "E4.19.0.20", {"center": v(7.54, -6.57) * mm, "radius": 0.3 * mm});
            skCircle(sketch, "E4.19.0.21", {"center": v(8.34, -6.57) * mm, "radius": 0.3 * mm});
            skCircle(sketch, "E4.20.0.0", {"center": v(-8.46, -7.37) * mm, "radius": 0.3 * mm});
            skCircle(sketch, "E4.20.0.1", {"center": v(-7.66, -7.37) * mm, "radius": 0.3 * mm});
            skCircle(sketch, "E4.20.0.2", {"center": v(-6.86, -7.37) * mm, "radius": 0.3 * mm});
            skCircle(sketch, "E4.20.0.3", {"center": v(-6.06, -7.37) * mm, "radius": 0.3 * mm});
            skCircle(sketch, "E4.20.0.4", {"center": v(-5.26, -7.37) * mm, "radius": 0.3 * mm});
            skCircle(sketch, "E4.20.0.5", {"center": v(-4.46, -7.37) * mm, "radius": 0.3 * mm});
            skCircle(sketch, "E4.20.0.6", {"center": v(-3.66, -7.37) * mm, "radius": 0.3 * mm});
            skCircle(sketch, "E4.20.0.7", {"center": v(-2.86, -7.37) * mm, "radius": 0.3 * mm});
            skCircle(sketch, "E4.20.0.8", {"center": v(-2.06, -7.37) * mm, "radius": 0.3 * mm});
            skCircle(sketch, "E4.20.0.9", {"center": v(-1.26, -7.37) * mm, "radius": 0.3 * mm});
            skCircle(sketch, "E4.20.0.10", {"center": v(-0.46, -7.37) * mm, "radius": 0.3 * mm});
            skCircle(sketch, "E4.20.0.11", {"center": v(0.34, -7.37) * mm, "radius": 0.3 * mm});
            skCircle(sketch, "E4.20.0.12", {"center": v(1.94, -7.37) * mm, "radius": 0.3 * mm});
            skCircle(sketch, "E4.20.0.13", {"center": v(2.74, -7.37) * mm, "radius": 0.3 * mm});
            skCircle(sketch, "E4.20.0.14", {"center": v(1.14, -7.37) * mm, "radius": 0.3 * mm});
            skCircle(sketch, "E4.20.0.15", {"center": v(3.54, -7.37) * mm, "radius": 0.3 * mm});
            skCircle(sketch, "E4.20.0.16", {"center": v(4.34, -7.37) * mm, "radius": 0.3 * mm});
            skCircle(sketch, "E4.20.0.17", {"center": v(5.14, -7.37) * mm, "radius": 0.3 * mm});
            skCircle(sketch, "E4.20.0.18", {"center": v(5.94, -7.37) * mm, "radius": 0.3 * mm});
            skCircle(sketch, "E4.20.0.19", {"center": v(6.74, -7.37) * mm, "radius": 0.3 * mm});
            skCircle(sketch, "E4.20.0.20", {"center": v(7.54, -7.37) * mm, "radius": 0.3 * mm});
            skCircle(sketch, "E4.20.0.21", {"center": v(8.34, -7.37) * mm, "radius": 0.3 * mm});
            skCircle(sketch, "E4.21.0.0", {"center": v(-8.46, -8.17) * mm, "radius": 0.3 * mm});
            skCircle(sketch, "E4.21.0.1", {"center": v(-7.66, -8.17) * mm, "radius": 0.3 * mm});
            skCircle(sketch, "E4.21.0.2", {"center": v(-6.86, -8.17) * mm, "radius": 0.3 * mm});
            skCircle(sketch, "E4.21.0.3", {"center": v(-6.06, -8.17) * mm, "radius": 0.3 * mm});
            skCircle(sketch, "E4.21.0.4", {"center": v(-5.26, -8.17) * mm, "radius": 0.3 * mm});
            skCircle(sketch, "E4.21.0.5", {"center": v(-4.46, -8.17) * mm, "radius": 0.3 * mm});
            skCircle(sketch, "E4.21.0.6", {"center": v(-3.66, -8.17) * mm, "radius": 0.3 * mm});
            skCircle(sketch, "E4.21.0.7", {"center": v(-2.86, -8.17) * mm, "radius": 0.3 * mm});
            skCircle(sketch, "E4.21.0.8", {"center": v(-2.06, -8.17) * mm, "radius": 0.3 * mm});
            skCircle(sketch, "E4.21.0.9", {"center": v(-1.26, -8.17) * mm, "radius": 0.3 * mm});
            skCircle(sketch, "E4.21.0.10", {"center": v(-0.46, -8.17) * mm, "radius": 0.3 * mm});
            skCircle(sketch, "E4.21.0.11", {"center": v(0.34, -8.17) * mm, "radius": 0.3 * mm});
            skCircle(sketch, "E4.21.0.12", {"center": v(1.94, -8.17) * mm, "radius": 0.3 * mm});
            skCircle(sketch, "E4.21.0.13", {"center": v(2.74, -8.17) * mm, "radius": 0.3 * mm});
            skCircle(sketch, "E4.21.0.14", {"center": v(1.14, -8.17) * mm, "radius": 0.3 * mm});
            skCircle(sketch, "E4.21.0.15", {"center": v(3.54, -8.17) * mm, "radius": 0.3 * mm});
            skCircle(sketch, "E4.21.0.16", {"center": v(4.34, -8.17) * mm, "radius": 0.3 * mm});
            skCircle(sketch, "E4.21.0.17", {"center": v(5.14, -8.17) * mm, "radius": 0.3 * mm});
            skCircle(sketch, "E4.21.0.18", {"center": v(5.94, -8.17) * mm, "radius": 0.3 * mm});
            skCircle(sketch, "E4.21.0.19", {"center": v(6.74, -8.17) * mm, "radius": 0.3 * mm});
            skCircle(sketch, "E4.21.0.20", {"center": v(7.54, -8.17) * mm, "radius": 0.3 * mm});
            skCircle(sketch, "E4.21.0.21", {"center": v(8.34, -8.17) * mm, "radius": 0.3 * mm});
            skLineSegment(sketch, "E4.direction1", {"start": v(-8.46, 8.63) * mm, "end": v(-8.46, 7.83) * mm, "construction": true});
            skSolve(sketch);
        }
        {
            var Q0;
            Q0 = qSketchRegion(id + "F4", true);
            extrude(context, id + "F5", {"entities" : qUnion([Q0]), "operationType" : NewBodyOperationType.ADD, "depth" : 0.25 * mm});
        }
    });
